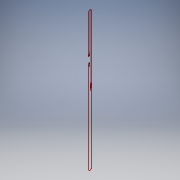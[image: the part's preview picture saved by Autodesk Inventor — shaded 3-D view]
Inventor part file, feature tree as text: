
AUTODESK INVENTOR PART (.ipt)
format: ipt  version: 2017 SP1 (Build 210196100, 196)  size: 313,856 bytes
history: native  units: in
note: dims shown in document units (in); Inventor stores cm internally (conversion verified against a paired STEP export)
features: extrude x1, fillet x1
ambient origin geometry x8: Origin, YZ Plane, XZ Plane, XY Plane, X Axis, Y Axis, Z Axis, Center Point
bodies: Solid1 (feature_tree)
feature tree (2):
  extrude  "Extrusion1"  Depth=0.375in
  fillet  "Fillet1"  Radius=0.1875in
